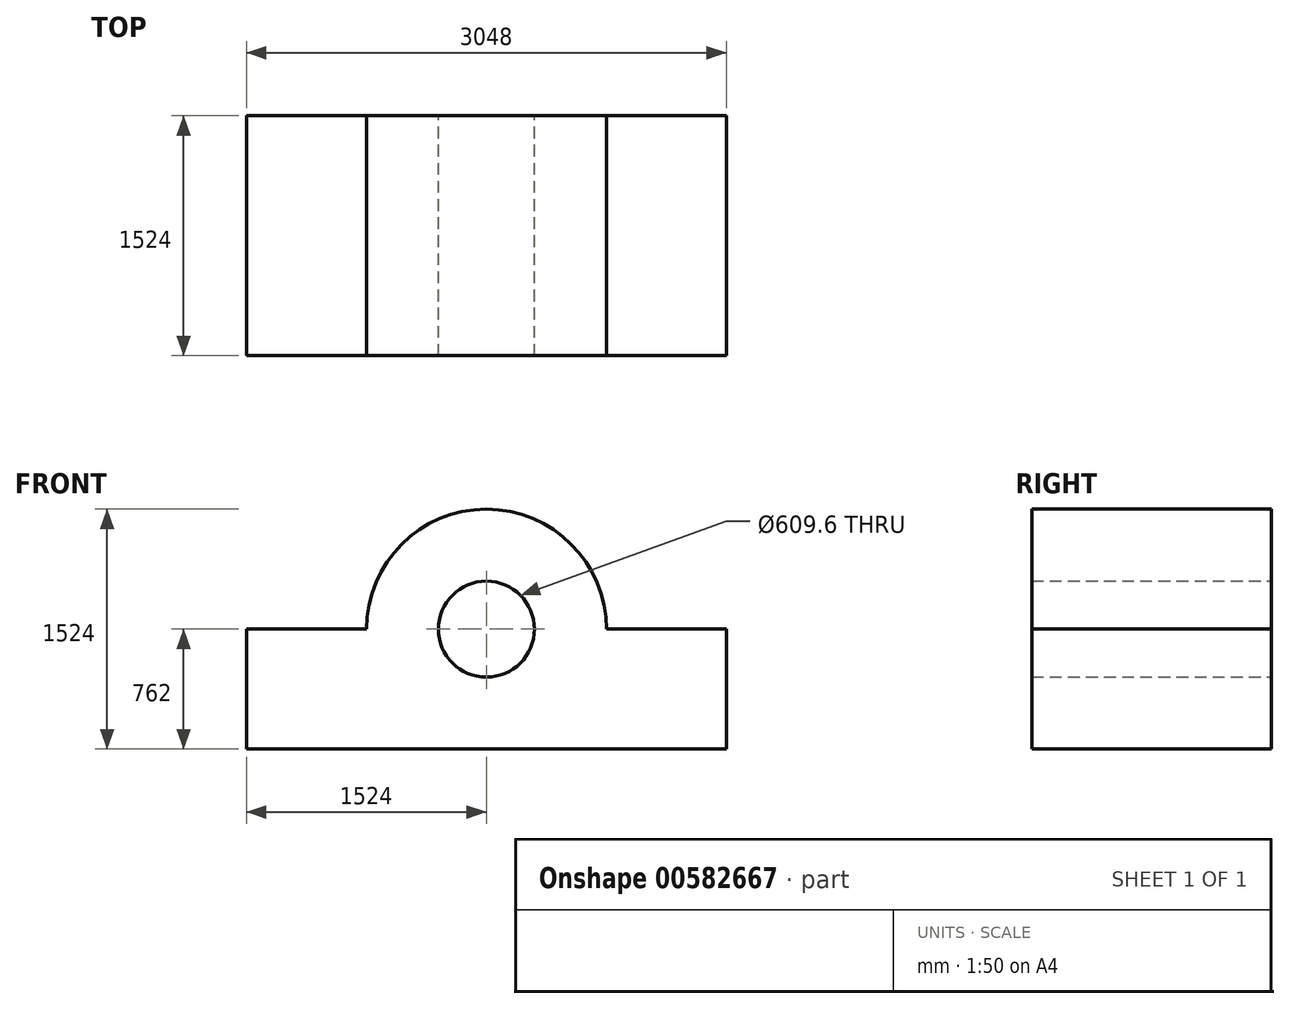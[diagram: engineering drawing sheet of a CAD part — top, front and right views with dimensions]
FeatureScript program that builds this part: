
annotation { "Feature Type Name" : "Feature", "Feature Type Description" : "" }
export const myFeature = defineFeature(function(context is Context, id is Id, definition is map)
    precondition{}
    {
        {
            var Q0;
            Q0=qCreatedBy(makeId("Front.planeOp"),FACE);
            var sketch = newSketch(context, id + "F0", { "sketchPlane" : qUnion([Q0])});
            skLineSegment(sketch, "E0", {"start": v(0, 0) * mm, "end": v(3048, 0) * mm});
            skLineSegment(sketch, "E1", {"start": v(3048, 0) * mm, "end": v(3048, 762) * mm});
            skLineSegment(sketch, "E2", {"start": v(3048, 762) * mm, "end": v(2286, 762) * mm});
            skLineSegment(sketch, "E3", {"start": v(0, 762) * mm, "end": v(0, 0) * mm});
            skCircle(sketch, "E4", {"center": v(1524, 762) * mm, "radius": 304.8 * mm});
            skArc(sketch, "E5", {"start": v(2286, 762) * mm, "mid": v(1524, 1524) * mm, "end": v(762, 762) * mm});
            skLineSegment(sketch, "E6.trimOffspring", {"start": v(762, 762) * mm, "end": v(0, 762) * mm});
            skSolve(sketch);
        }
        {
            var Q0;
            Q0 = qSketchRegion(id + "F0", true);
            extrude(context, id + "F1", {"entities" : qUnion([Q0]), "depth" : 1524 * mm, "offsetDistance" : 25.4 * mm});
        }
    });
